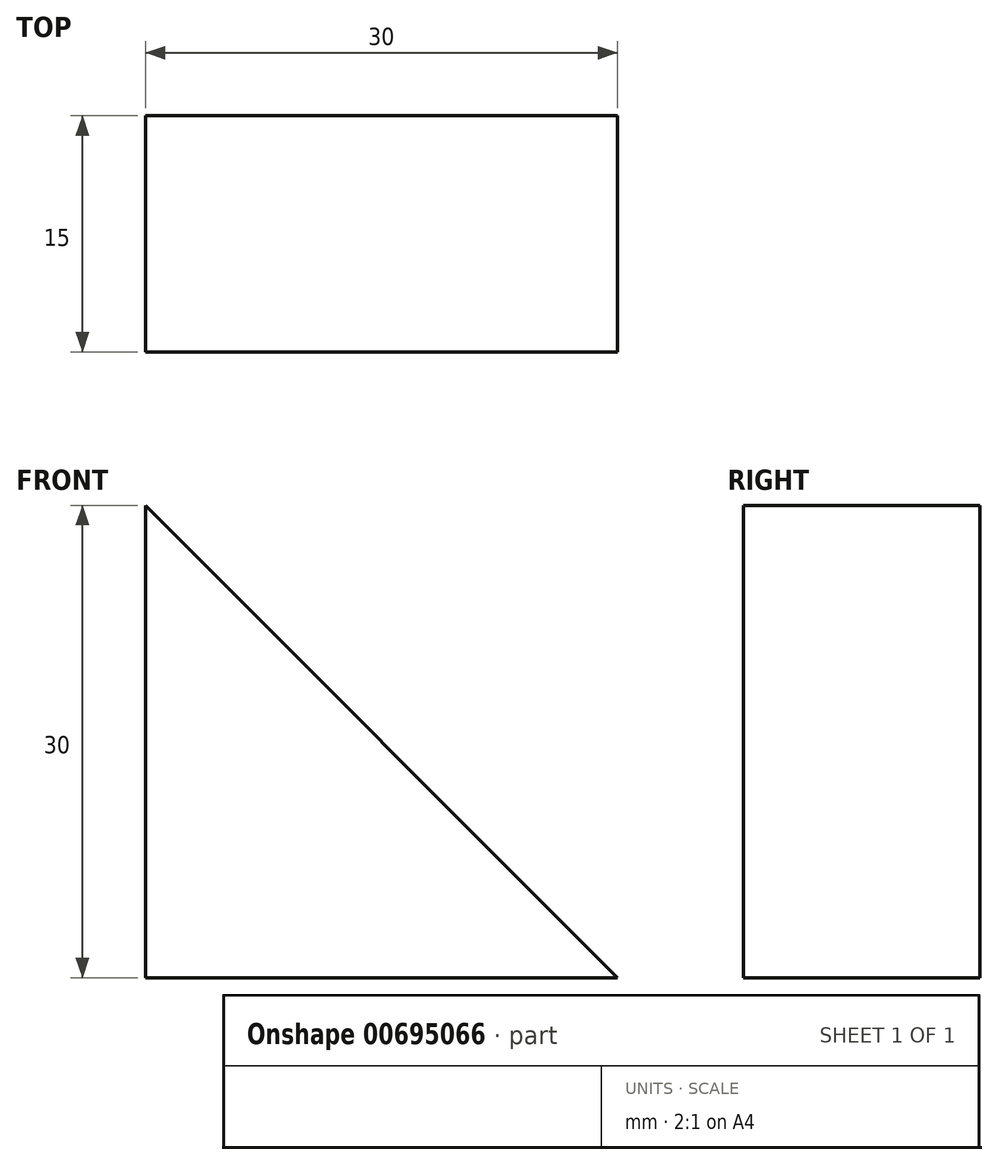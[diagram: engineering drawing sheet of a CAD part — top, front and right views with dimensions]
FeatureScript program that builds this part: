
annotation { "Feature Type Name" : "Feature", "Feature Type Description" : "" }
export const myFeature = defineFeature(function(context is Context, id is Id, definition is map)
    precondition{}
    {
        {
            var Q0;
            Q0=qCreatedBy(makeId("Front.planeOp"),FACE);
            var sketch = newSketch(context, id + "F0", { "sketchPlane" : qUnion([Q0])});
            skLineSegment(sketch, "E0", {"start": v(0, 0) * mm, "end": v(0, 30) * mm});
            skLineSegment(sketch, "E1", {"start": v(0, 0) * mm, "end": v(30, 0) * mm});
            skLineSegment(sketch, "E2", {"start": v(30, 0) * mm, "end": v(0, 30) * mm});
            skSolve(sketch);
        }
        {
            var Q0;
            Q0=makeQuery(id+"F0.imprint","IMPRINT",FACE,{"disambiguationData":[TD([[makeQuery(id+"F0.imprint","IMPRINT",EDGE,{"derivedFrom":sQuery(id+"F0.wireOp",EDGE,"E0")}),-1.0]])]});
            extrude(context, id + "F1", {"entities" : qUnion([Q0]), "oppositeDirection" : true, "depth" : 15 * mm, "offsetDistance" : 25 * mm});
        }
        {
            var Q0;
            Q0=makeQuery(id+"F1.opExtrude","CAP_FACE",FACE,{"disambiguationData":[OSD([sQuery(id+"F0.wireOp",EDGE,"E0"),sQuery(id+"F0.wireOp",EDGE,"E1"),sQuery(id+"F0.wireOp",EDGE,"E2")])],"isStart":true});
            cPlane(context, id + "F2", {"entities" : qUnion([Q0]), "cplaneType" : CPlaneType.OFFSET, "offset" : 15 * mm, "oppositeDirection" : true, "width" : 150 * mm, "height" : 150 * mm});
        }
    });
